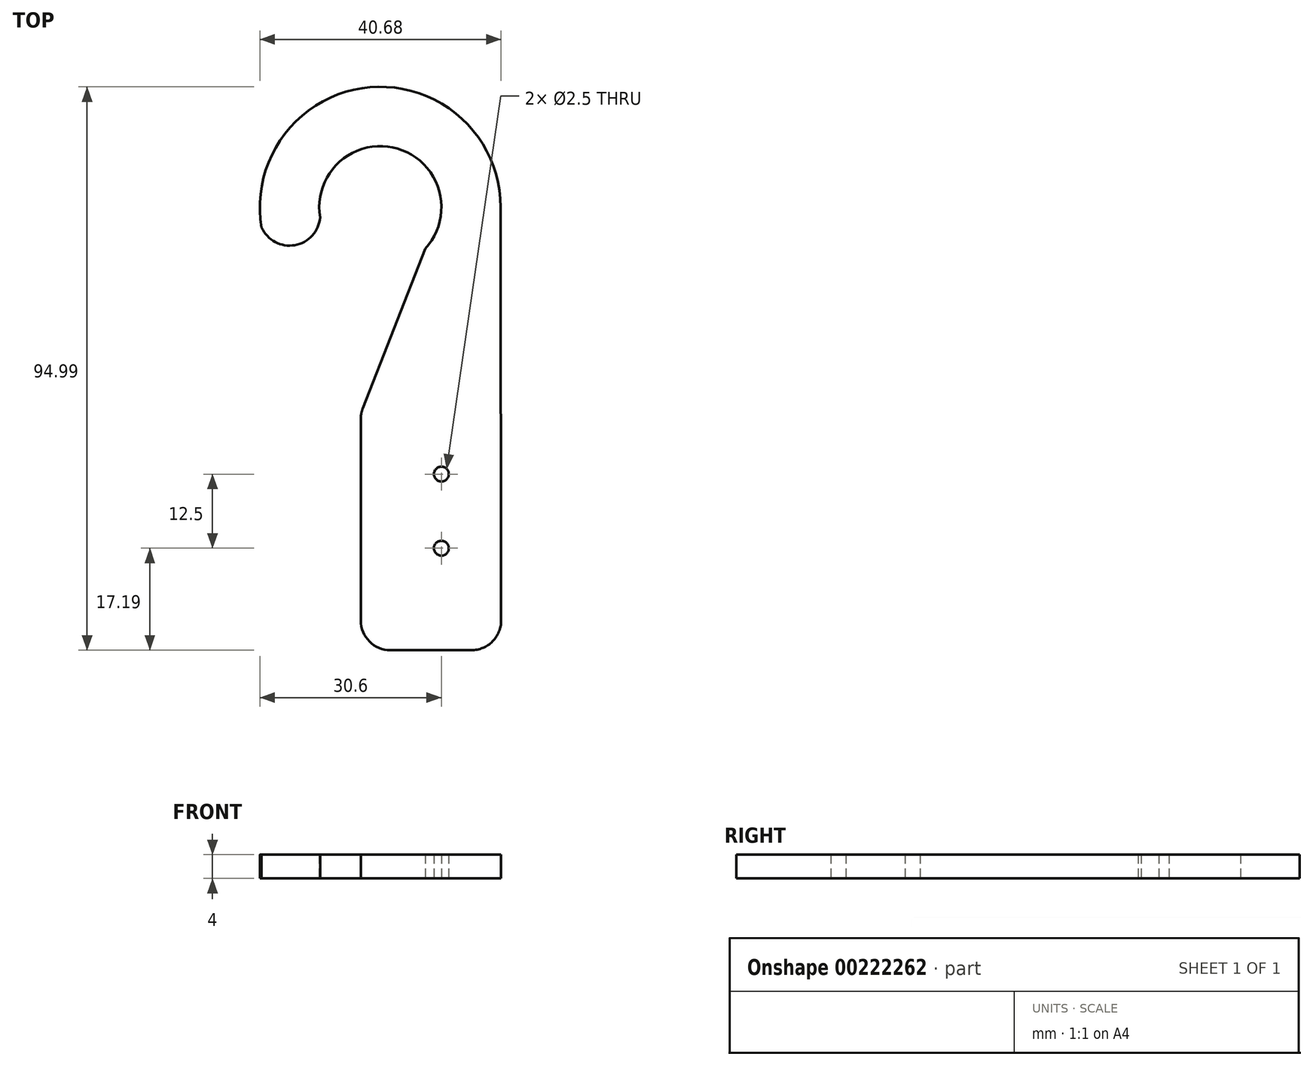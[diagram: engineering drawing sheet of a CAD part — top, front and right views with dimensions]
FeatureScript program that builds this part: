
annotation { "Feature Type Name" : "Feature", "Feature Type Description" : "" }
export const myFeature = defineFeature(function(context is Context, id is Id, definition is map)
    precondition{}
    {
        {
            var Q0;
            Q0=qCreatedBy(makeId("Top.planeOp"),FACE);
            var sketch = newSketch(context, id + "F0", { "sketchPlane" : qUnion([Q0])});
            skPoint(sketch, "E0", {"position": v(-10.3, 0) * mm});
            skCircle(sketch, "E1", {"center": v(-10.3, 0) * mm, "radius": 10.3 * mm});
            skPoint(sketch, "E2", {"position": v(0, -45) * mm});
            skPoint(sketch, "E3", {"position": v(0, -57.5) * mm});
            skCircle(sketch, "E4", {"center": v(0, -45) * mm, "radius": 1.25 * mm});
            skCircle(sketch, "E5", {"center": v(0, -57.5) * mm, "radius": 1.25 * mm});
            skCircle(sketch, "E6", {"center": v(-10.3, 0) * mm, "radius": 20.3 * mm});
            skLineSegment(sketch, "E7", {"start": v(0, 0) * mm, "end": v(-13.59, -34.8) * mm});
            skLineSegment(sketch, "E8", {"start": v(-13.59, -34.8) * mm, "end": v(-13.59, -74.7) * mm});
            skLineSegment(sketch, "E9", {"start": v(-13.59, -74.7) * mm, "end": v(10.08, -74.7) * mm});
            skLineSegment(sketch, "E10", {"start": v(10.08, -74.7) * mm, "end": v(10, 0) * mm});
            skCircle(sketch, "E11", {"center": v(-25.6, -1.3) * mm, "radius": 5.17 * mm});
            skPoint(sketch, "E11.first.point", {"position": v(-30.6, 0) * mm});
            skPoint(sketch, "E11.second.point", {"position": v(-20.6, 0) * mm});
            skPoint(sketch, "E11.third.point", {"position": v(-23.26, -5.92) * mm});
            skSolve(sketch);
        }
        {
            var Q0;
            {var subQ2=sQuery(id+"F0.wireOp",EDGE,"E7");var subQ6=sQuery(id+"F0.wireOp",EDGE,"E1");var subQ7=makeQuery(id+"F0.imprint","INTERSECT",VERTEX,{"disambiguationData":[OD(0.0)],"derivedFrom":[subQ6,subQ2]});Q0=makeQuery(id+"F0.imprint","IMPRINT",FACE,{"disambiguationData":[TD([[makeQuery(id+"F0.imprint","IMPRINT",EDGE,{"disambiguationData":[TD([[subQ7,-1.0]])],"derivedFrom":subQ6}),-1.0]])]});}
            var Q1;
            {var subQ0=sQuery(id+"F0.wireOp",EDGE,"E11");var subQ1=sQuery(id+"F0.wireOp",EDGE,"E1");var subQ2=makeQuery(id+"F0.imprint","INTERSECT",VERTEX,{"disambiguationData":[OD(0.0)],"derivedFrom":[subQ1,subQ0]});Q1=makeQuery(id+"F0.imprint","IMPRINT",FACE,{"disambiguationData":[TD([[makeQuery(id+"F0.imprint","IMPRINT",EDGE,{"disambiguationData":[TD([[subQ2,-1.0]])],"derivedFrom":subQ1}),-1.0]])]});}
            var Q2;
            Q2=makeQuery(id+"F0.imprint","IMPRINT",FACE,{"disambiguationData":[TD([[makeQuery(id+"F0.imprint","IMPRINT",EDGE,{"derivedFrom":sQuery(id+"F0.wireOp",EDGE,"E4")}),-1.0]])]});
            extrude(context, id + "F1", {"entities" : qUnion([Q0, Q1, Q2]), "depth" : 4 * mm});
        }
        {
            var Q0;
            Q0=makeQuery(id+"F1.opExtrude","SWEPT_EDGE",EDGE,{"disambiguationData":[OSD([sQuery(id+"F0.wireOp",EDGE,"E8"),sQuery(id+"F0.wireOp",EDGE,"E9")])]});
            fillet(context, id + "F2", {"entities" : qUnion([Q0]), "radius" : 5 * mm, "tangentPropagation" : true, "allowEdgeOverflow" : false});
        }
        {
            var Q0;
            Q0=makeQuery(id+"F1.opExtrude","SWEPT_EDGE",EDGE,{"disambiguationData":[OSD([sQuery(id+"F0.wireOp",EDGE,"E9"),sQuery(id+"F0.wireOp",EDGE,"E10")])]});
            fillet(context, id + "F3", {"entities" : qUnion([Q0]), "radius" : 5 * mm, "tangentPropagation" : true, "allowEdgeOverflow" : false});
        }
        {
            var Q0;
            Q0=makeQuery(id+"F1.opExtrude","SWEPT_EDGE",EDGE,{"disambiguationData":[OSD([sQuery(id+"F0.wireOp",EDGE,"E7"),sQuery(id+"F0.wireOp",EDGE,"E8")])]});
            fillet(context, id + "F4", {"entities" : qUnion([Q0]), "radius" : 5 * mm, "tangentPropagation" : true, "allowEdgeOverflow" : false});
        }
    });
